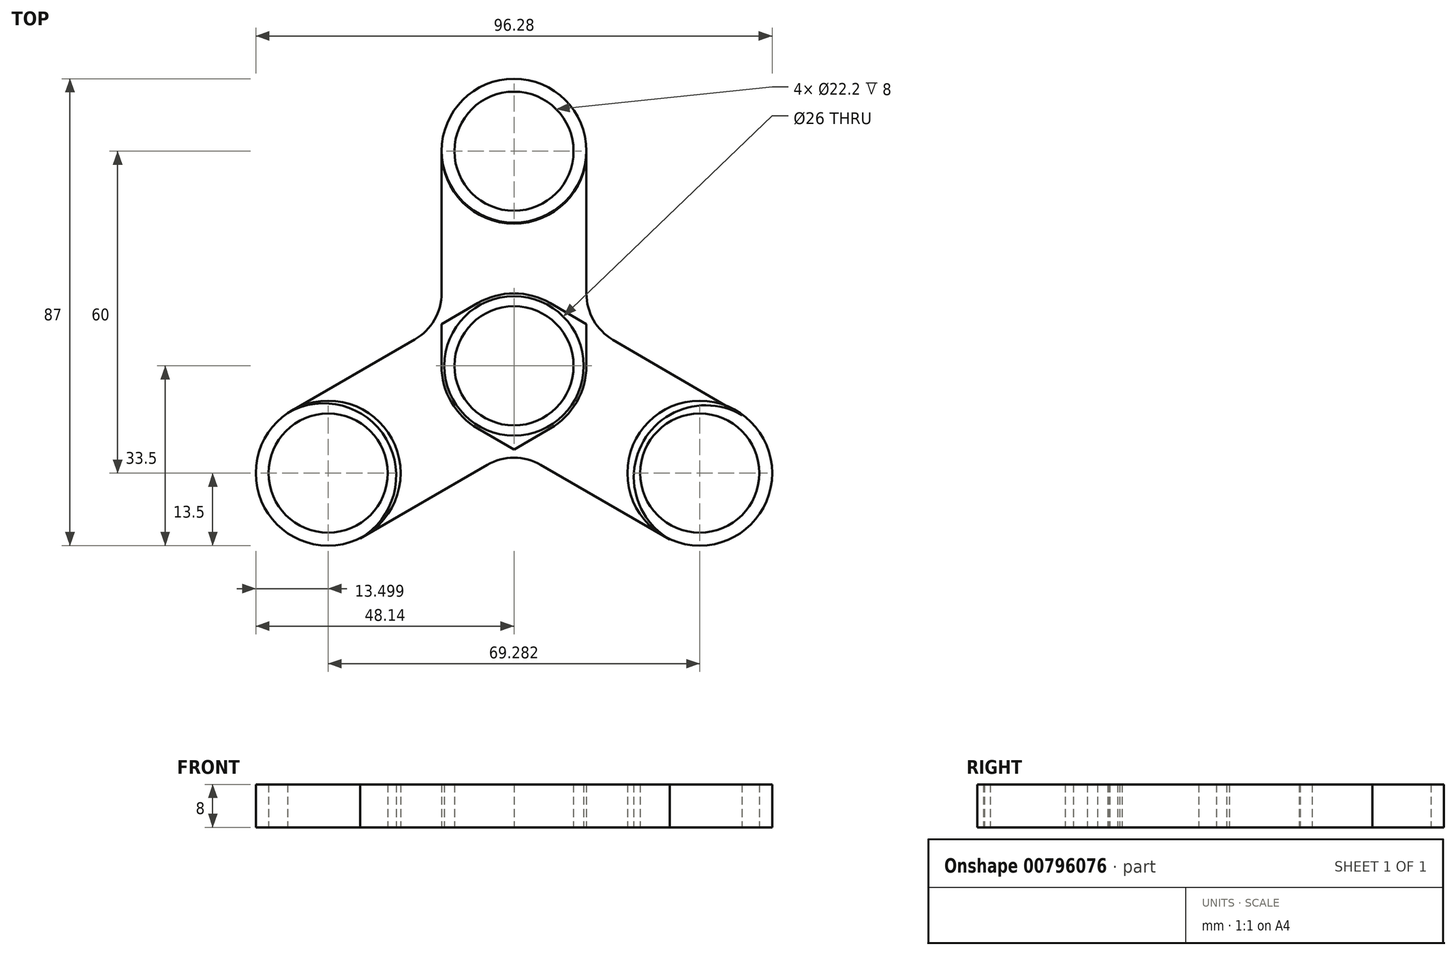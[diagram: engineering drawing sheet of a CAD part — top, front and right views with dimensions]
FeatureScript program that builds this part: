
annotation { "Feature Type Name" : "Feature", "Feature Type Description" : "" }
export const myFeature = defineFeature(function(context is Context, id is Id, definition is map)
    precondition{}
    {
        {
            var Q0;
            Q0=qCreatedBy(makeId("Top.planeOp"),FACE);
            var sketch = newSketch(context, id + "F0", { "sketchPlane" : qUnion([Q0])});
            skCircle(sketch, "E0", {"center": v(0, 0) * mm, "radius": 13.5 * mm});
            skCircle(sketch, "E1", {"center": v(0, 40) * mm, "radius": 13.5 * mm});
            skCircle(sketch, "E2.1.0", {"center": v(-34.64, -20) * mm, "radius": 13.5 * mm});
            skCircle(sketch, "E2.2.0", {"center": v(34.64, -20) * mm, "radius": 13.5 * mm});
            skCircle(sketch, "E3", {"center": v(0, 40) * mm, "radius": 11.1 * mm});
            skCircle(sketch, "E4", {"center": v(34.64, -20) * mm, "radius": 11.1 * mm});
            skCircle(sketch, "E5", {"center": v(-34.64, -20) * mm, "radius": 11.1 * mm});
            skCircle(sketch, "E6", {"center": v(0, 0) * mm, "radius": 11.1 * mm});
            skPoint(sketch, "E7.orphan", {"position": v(-46.33, -13.25) * mm});
            skPoint(sketch, "E8.orphan", {"position": v(34.64, -33.5) * mm});
            skPoint(sketch, "E9.orphan", {"position": v(-11.7, 46.75) * mm});
            skPoint(sketch, "E10.orphan", {"position": v(11.7, 46.75) * mm});
            skLineSegment(sketch, "E11", {"start": v(-13.5, 40) * mm, "end": v(-13.5, 0) * mm});
            skLineSegment(sketch, "E12", {"start": v(13.5, 0) * mm, "end": v(13.5, 40) * mm});
            skLineSegment(sketch, "E13", {"start": v(-6.75, 11.7) * mm, "end": v(-41.4, -8.3) * mm});
            skLineSegment(sketch, "E14", {"start": v(-27.9, -31.7) * mm, "end": v(6.75, -11.7) * mm});
            skLineSegment(sketch, "E15", {"start": v(-6.75, -11.7) * mm, "end": v(27.9, -31.7) * mm});
            skLineSegment(sketch, "E16", {"start": v(41.4, -8.3) * mm, "end": v(6.75, 11.7) * mm});
            skSolve(sketch);
        }
        {
            var Q0;
            Q0=qCreatedBy(makeId("Top.planeOp"),FACE);
            var sketch = newSketch(context, id + "F1", { "sketchPlane" : qUnion([Q0])});
            skLineSegment(sketch, "E17", {"start": v(-42.2, -8.78) * mm, "end": v(-18.5, 4.9) * mm});
            skLineSegment(sketch, "E18", {"start": v(-28.7, -32.16) * mm, "end": v(-5, -18.48) * mm});
            skLineSegment(sketch, "E19", {"start": v(18.46, 4.86) * mm, "end": v(42.5, -9.18) * mm});
            skLineSegment(sketch, "E20", {"start": v(29.04, -32.36) * mm, "end": v(5, -18.48) * mm});
            skLineSegment(sketch, "E21", {"start": v(-13.5, 40.18) * mm, "end": v(-13.5, 13.57) * mm});
            skLineSegment(sketch, "E22", {"start": v(13.5, 40.18) * mm, "end": v(13.5, 13.5) * mm});
            skPoint(sketch, "E23.orphan", {"position": v(-13.5, 0) * mm});
            skPoint(sketch, "E24.orphan", {"position": v(13.5, 0) * mm});
            skPoint(sketch, "E25.visualSharp", {"position": v(-13.5, 7.8) * mm});
            skArc(sketch, "E25.filletArc", {"start": v(-18.5, 4.9) * mm, "mid": v(-14.84, 8.57) * mm, "end": v(-13.5, 13.57) * mm});
            skPoint(sketch, "E26.visualSharp", {"position": v(13.5, 7.75) * mm});
            skArc(sketch, "E26.filletArc", {"start": v(13.5, 13.5) * mm, "mid": v(14.83, 8.51) * mm, "end": v(18.46, 4.86) * mm});
            skPoint(sketch, "E27.visualSharp", {"position": v(0, -15.59) * mm});
            skArc(sketch, "E27.filletArc", {"start": v(5, -18.48) * mm, "mid": v(0, -17.14) * mm, "end": v(-5, -18.48) * mm});
            skArc(sketch, "E28", {"start": v(-13.5, 40.18) * mm, "mid": v(0, 26.68) * mm, "end": v(13.5, 40.18) * mm});
            skPoint(sketch, "E28.third.point", {"position": v(0, 53.68) * mm});
            skPoint(sketch, "E28.third.point.positionSnap0", {"position": v(0, 40.18) * mm});
            skArc(sketch, "E29", {"start": v(42.5, -9.18) * mm, "mid": v(24.15, -14.02) * mm, "end": v(29.04, -32.36) * mm});
            skPoint(sketch, "E29.third.point", {"position": v(47.1, -27.85) * mm});
            skArc(sketch, "E30", {"start": v(-28.7, -32.16) * mm, "mid": v(-23.77, -13.72) * mm, "end": v(-42.2, -8.78) * mm});
            skPoint(sketch, "E30.third.point", {"position": v(-48.06, -25.32) * mm});
            skPoint(sketch, "E30.third.point.positionSnap0", {"position": v(-16.85, -25.32) * mm});
            skCircle(sketch, "E31", {"center": v(0, 0) * mm, "radius": 13 * mm});
            skSolve(sketch);
        }
        {
            var Q0;
            Q0=makeQuery(id+"F1.imprint","IMPRINT",FACE,{"disambiguationData":[TD([[makeQuery(id+"F1.imprint","IMPRINT",EDGE,{"derivedFrom":sQuery(id+"F1.wireOp",EDGE,"E17")}),-1.0]])]});
            extrude(context, id + "F2", {"entities" : qUnion([Q0]), "endBound" : BoundingType.SYMMETRIC, "depth" : 8 * mm, "offsetDistance" : 25 * mm});
        }
        {
            var Q0;
            Q0=makeQuery(id+"F0.imprint","IMPRINT",FACE,{"disambiguationData":[TD([[makeQuery(id+"F0.imprint","IMPRINT",EDGE,{"derivedFrom":sQuery(id+"F0.wireOp",EDGE,"E1")}),1.0]])]});
            var Q1;
            Q1=makeQuery(id+"F0.imprint","IMPRINT",FACE,{"disambiguationData":[TD([[makeQuery(id+"F0.imprint","IMPRINT",EDGE,{"derivedFrom":sQuery(id+"F0.wireOp",EDGE,"E2.2.0")}),1.0]])]});
            var Q2;
            Q2=makeQuery(id+"F0.imprint","IMPRINT",FACE,{"disambiguationData":[TD([[makeQuery(id+"F0.imprint","IMPRINT",EDGE,{"derivedFrom":sQuery(id+"F0.wireOp",EDGE,"E2.1.0")}),1.0]])]});
            var Q3;
            Q3=makeQuery(id+"F0.imprint","IMPRINT",FACE,{"disambiguationData":[TD([[makeQuery(id+"F0.imprint","IMPRINT",EDGE,{"derivedFrom":sQuery(id+"F0.wireOp",EDGE,"E0")}),1.0]])]});
            var Q4;
            Q4=makeQuery(id+"F0.imprint","IMPRINT",FACE,{"disambiguationData":[TD([[makeQuery(id+"F0.imprint","IMPRINT",EDGE,{"derivedFrom":sQuery(id+"F0.wireOp",EDGE,"E0")}),-1.0]])]});
            extrude(context, id + "F3", {"entities" : qUnion([Q0, Q1, Q2, Q3, Q4]), "endBound" : BoundingType.SYMMETRIC, "depth" : 8 * mm, "offsetDistance" : 25 * mm});
        }
    });
